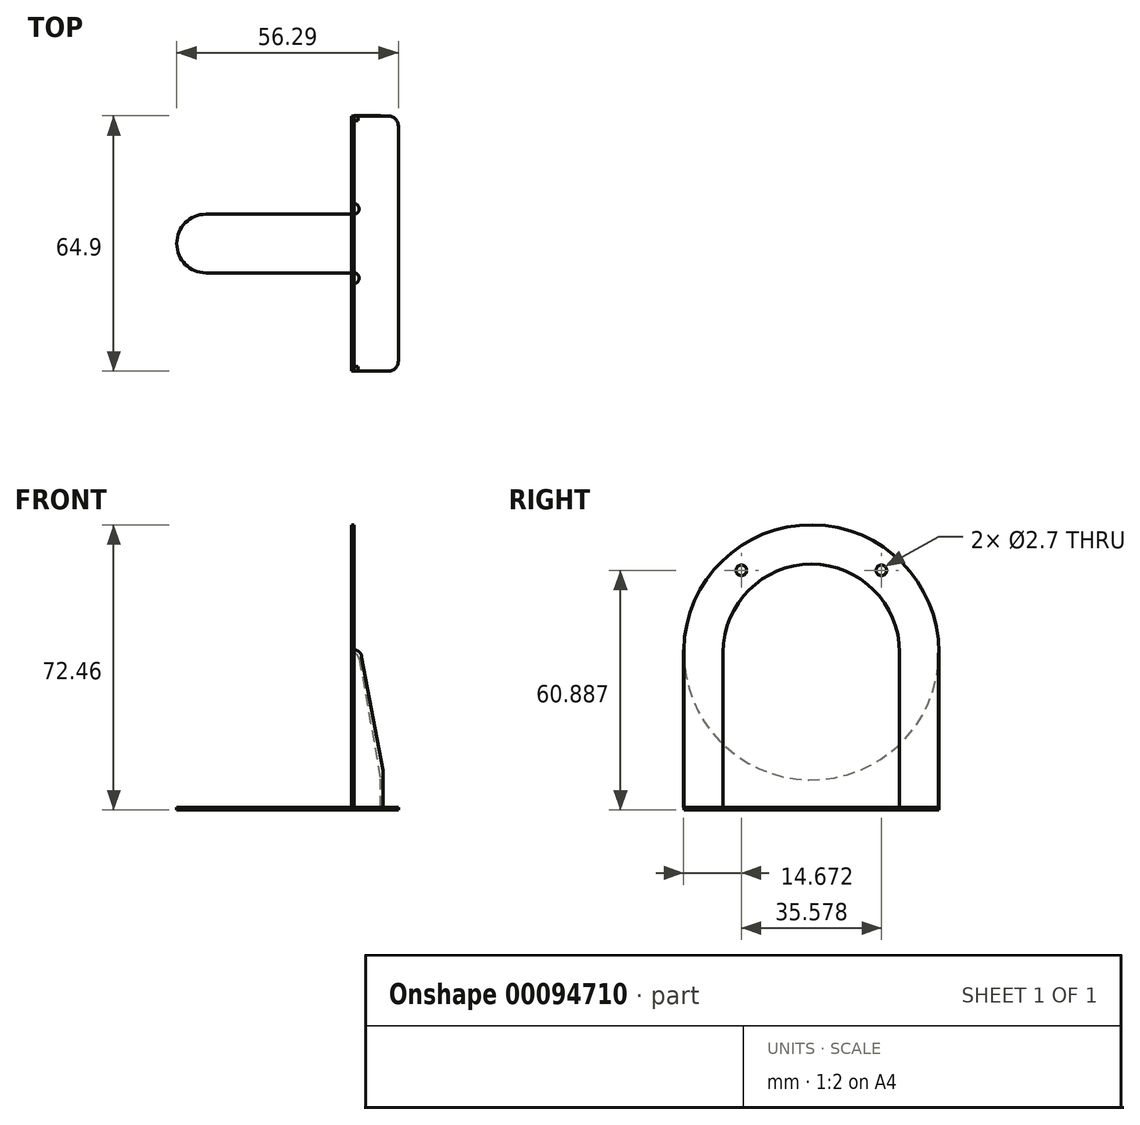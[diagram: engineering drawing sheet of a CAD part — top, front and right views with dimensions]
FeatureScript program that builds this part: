
annotation { "Feature Type Name" : "Feature", "Feature Type Description" : "" }
export const myFeature = defineFeature(function(context is Context, id is Id, definition is map)
    precondition{}
    {
        {
            var Q0;
            Q0=qCreatedBy(makeId("Top.planeOp"),FACE);
            var sketch = newSketch(context, id + "F0", { "sketchPlane" : qUnion([Q0])});
            skLineSegment(sketch, "E0", {"start": v(-33.32, 0) * mm, "end": v(45.54, 0) * mm, "construction": true});
            skLineSegment(sketch, "E1.bottom", {"start": v(-33.32, 0) * mm, "end": v(11.68, 0) * mm});
            skLineSegment(sketch, "E1.top", {"start": v(-33.32, -14.9) * mm, "end": v(11.68, -14.9) * mm});
            skLineSegment(sketch, "E1.left", {"start": v(-33.32, 0) * mm, "end": v(-33.32, -14.9) * mm});
            skLineSegment(sketch, "E1.right", {"start": v(11.68, 0) * mm, "end": v(11.68, -14.9) * mm});
            skLineSegment(sketch, "E2.bottom", {"start": v(11.68, 24.95) * mm, "end": v(22.97, 24.95) * mm});
            skLineSegment(sketch, "E2.top", {"start": v(11.68, -39.85) * mm, "end": v(22.97, -39.85) * mm});
            skLineSegment(sketch, "E2.right", {"start": v(22.97, 24.95) * mm, "end": v(22.97, -39.85) * mm});
            skLineSegment(sketch, "E3", {"start": v(11.68, 24.95) * mm, "end": v(11.68, 0) * mm});
            skLineSegment(sketch, "E4", {"start": v(11.68, -14.9) * mm, "end": v(11.68, -39.85) * mm});
            skSolve(sketch);
        }
        {
            var Q0;
            Q0=makeQuery(id+"F0.imprint","IMPRINT",FACE,{"disambiguationData":[TD([[makeQuery(id+"F0.imprint","IMPRINT",EDGE,{"derivedFrom":sQuery(id+"F0.wireOp",EDGE,"E1.bottom")}),-1.0]])]});
            extrude(context, id + "F1", {"entities" : qUnion([Q0]), "depth" : 0.63 * mm});
        }
        {
            var Q0;
            Q0=makeQuery(id+"F1.opExtrude","SWEPT_EDGE",EDGE,{"disambiguationData":[OSD([sQuery(id+"F0.wireOp",EDGE,"E1.bottom"),sQuery(id+"F0.wireOp",EDGE,"E1.left")])]});
            fillet(context, id + "F2", {"entities" : qUnion([Q0]), "radius" : 7.4 * mm, "tangentPropagation" : true, "allowEdgeOverflow" : false});
        }
        {
            var Q0;
            Q0=makeQuery(id+"F1.opExtrude","SWEPT_EDGE",EDGE,{"disambiguationData":[OSD([sQuery(id+"F0.wireOp",EDGE,"E1.top"),sQuery(id+"F0.wireOp",EDGE,"E1.left")])]});
            fillet(context, id + "F3", {"entities" : qUnion([Q0]), "radius" : 7.4 * mm, "tangentPropagation" : true, "allowEdgeOverflow" : false});
        }
        {
            var Q0;
            Q0=makeQuery(id+"F0.imprint","IMPRINT",FACE,{"disambiguationData":[TD([[makeQuery(id+"F0.imprint","IMPRINT",EDGE,{"derivedFrom":sQuery(id+"F0.wireOp",EDGE,"E1.right")}),1.0]])]});
            extrude(context, id + "F4", {"entities" : qUnion([Q0]), "operationType" : NewBodyOperationType.ADD, "depth" : 0.63 * mm});
        }
        {
            var Q0;
            {var subQ0=sQuery(id+"F0.wireOp",EDGE,"E1.right");Q0=makeQuery(id+"F4.boolean.opBoolean","MERGE",FACE,{"derivedFrom":[makeQuery(id+"F1.opExtrude","CAP_FACE",FACE,{"disambiguationData":[OSD([sQuery(id+"F0.wireOp",EDGE,"E1.bottom"),sQuery(id+"F0.wireOp",EDGE,"E1.top"),sQuery(id+"F0.wireOp",EDGE,"E1.left"),subQ0])],"isStart":false}),makeQuery(id+"F4.opExtrude","CAP_FACE",FACE,{"disambiguationData":[OSD([subQ0,sQuery(id+"F0.wireOp",EDGE,"E2.bottom"),sQuery(id+"F0.wireOp",EDGE,"E2.top"),sQuery(id+"F0.wireOp",EDGE,"E2.right"),sQuery(id+"F0.wireOp",EDGE,"E3"),sQuery(id+"F0.wireOp",EDGE,"E4")])],"isStart":false})]});}
            var sketch = newSketch(context, id + "F5", { "sketchPlane" : qUnion([Q0])});
            skLineSegment(sketch, "E5.bottom", {"start": v(11.68, -39.85) * mm, "end": v(12.78, -39.85) * mm});
            skLineSegment(sketch, "E5.top", {"start": v(11.68, -38.75) * mm, "end": v(12.78, -38.75) * mm});
            skLineSegment(sketch, "E5.left", {"start": v(11.68, -39.85) * mm, "end": v(11.68, -38.75) * mm});
            skLineSegment(sketch, "E5.right", {"start": v(12.78, -39.85) * mm, "end": v(12.78, -38.75) * mm});
            skLineSegment(sketch, "E6.bottom", {"start": v(11.68, 24.95) * mm, "end": v(12.78, 24.95) * mm});
            skLineSegment(sketch, "E6.top", {"start": v(11.68, 23.85) * mm, "end": v(12.78, 23.85) * mm});
            skLineSegment(sketch, "E6.left", {"start": v(11.68, 24.95) * mm, "end": v(11.68, 23.85) * mm});
            skLineSegment(sketch, "E6.right", {"start": v(12.78, 24.95) * mm, "end": v(12.78, 23.85) * mm});
            skArc(sketch, "E7", {"start": v(11.68, -17.6) * mm, "mid": v(13.03, -16.25) * mm, "end": v(11.68, -14.9) * mm});
            skArc(sketch, "E8", {"start": v(11.68, 0) * mm, "mid": v(13.03, 1.35) * mm, "end": v(11.68, 2.7) * mm});
            skSolve(sketch);
        }
        {
            var Q0;
            {var subQ0=sQuery(id+"F0.wireOp",EDGE,"E1.right");var subQ3=sQuery(id+"F0.wireOp",EDGE,"E1.bottom");var subQ4=sQuery(id+"F0.wireOp",EDGE,"E4");var subQ5=sQuery(id+"F0.wireOp",EDGE,"E3");Q0=makeQuery(id+"F4.boolean.opBoolean","SPLIT",FACE,{"disambiguationData":[TD([makeQuery(id+"F1.opExtrude","SWEPT_FACE",FACE,{"disambiguationData":[OSD([subQ3])]})])],"derivedFrom":makeQuery(id+"F4.opExtrude","SWEPT_FACE",FACE,{"disambiguationData":[OSD([subQ0,subQ5,subQ4])]})});}
            var sketch = newSketch(context, id + "F6", { "sketchPlane" : qUnion([Q0])});
            skLineSegment(sketch, "E9.bottom", {"start": v(39.85, 0) * mm, "end": v(29.85, 0) * mm});
            skLineSegment(sketch, "E9.top", {"start": v(39.85, 40.06) * mm, "end": v(29.85, 40.06) * mm});
            skLineSegment(sketch, "E9.left", {"start": v(39.85, 0) * mm, "end": v(39.85, 40.06) * mm});
            skLineSegment(sketch, "E9.right", {"start": v(29.85, 0) * mm, "end": v(29.85, 40.06) * mm});
            skLineSegment(sketch, "E10.bottom", {"start": v(-24.95, 0) * mm, "end": v(-14.95, 0) * mm});
            skLineSegment(sketch, "E10.top", {"start": v(-24.95, 40.06) * mm, "end": v(-14.95, 40.06) * mm});
            skLineSegment(sketch, "E10.left", {"start": v(-24.95, 0) * mm, "end": v(-24.95, 40.06) * mm});
            skLineSegment(sketch, "E10.right", {"start": v(-14.95, 0) * mm, "end": v(-14.95, 40.06) * mm});
            skArc(sketch, "E11", {"start": v(39.85, 40.06) * mm, "mid": v(7.45, 72.46) * mm, "end": v(-24.95, 40.06) * mm});
            skArc(sketch, "E12", {"start": v(29.85, 40.06) * mm, "mid": v(7.45, 62.46) * mm, "end": v(-14.95, 40.06) * mm});
            skSolve(sketch);
        }
        {
            var Q0;
            Q0=makeQuery(id+"F6.imprint","IMPRINT",FACE,{"disambiguationData":[TD([[makeQuery(id+"F6.imprint","IMPRINT",EDGE,{"derivedFrom":sQuery(id+"F6.wireOp",EDGE,"E9.bottom")}),-1.0]])]});
            var Q1;
            {var subQ0=sQuery(id+"F6.wireOp",EDGE,"E10.top");Q1=makeQuery(id+"F6.imprint","IMPRINT",FACE,{"disambiguationData":[TD([[makeQuery(id+"F6.imprint","IMPRINT",EDGE,{"derivedFrom":subQ0}),-1.0]])]});}
            extrude(context, id + "F7", {"entities" : qUnion([Q0, Q1]), "operationType" : NewBodyOperationType.ADD, "depth" : 0.63 * mm});
        }
        {
            var Q0;
            Q0 = qSketchRegion(id + "F6", true);
            extrude(context, id + "F8", {"entities" : qUnion([Q0]), "operationType" : NewBodyOperationType.ADD, "depth" : 0.63 * mm});
        }
        {
            var Q0;
            Q0=makeQuery(id+"F7.boolean.opBoolean","MERGE",FACE,{"derivedFrom":[makeQuery(id+"F4.opExtrude","SWEPT_FACE",FACE,{"disambiguationData":[OSD([sQuery(id+"F0.wireOp",EDGE,"E2.top")])]}),makeQuery(id+"F7.opExtrude","SWEPT_FACE",FACE,{"disambiguationData":[OSD([sQuery(id+"F6.wireOp",EDGE,"E9.left")])]})]});
            var sketch = newSketch(context, id + "F9", { "sketchPlane" : qUnion([Q0])});
            skLineSegment(sketch, "E13", {"start": v(11.68, 0.63) * mm, "end": v(11.68, 40.7) * mm});
            skLineSegment(sketch, "E14", {"start": v(19.08, 0) * mm, "end": v(19.08, 10.06) * mm});
            skPoint(sketch, "E15", {"position": v(11.68, 36.69) * mm});
            skPoint(sketch, "E16", {"position": v(11.68, 36.7) * mm});
            skArc(sketch, "E17", {"start": v(11.68, 36.7) * mm, "mid": v(13.7, 38.7) * mm, "end": v(11.68, 40.7) * mm});
            skLineSegment(sketch, "E18", {"start": v(13.7, 38.7) * mm, "end": v(19.08, 10.06) * mm});
            skSolve(sketch);
        }
        {
            var Q0;
            {var subQ0=sQuery(id+"F9.wireOp",EDGE,"E18");Q0=makeQuery(id+"F9.imprint","IMPRINT",FACE,{"disambiguationData":[TD([[makeQuery(id+"F9.imprint","IMPRINT",EDGE,{"derivedFrom":subQ0}),-1.0]])]});}
            var Q1;
            {var subQ0=sQuery(id+"F9.wireOp",EDGE,"E13");var subQ5=sQuery(id+"F9.wireOp",EDGE,"E17");var subQ6=makeQuery(id+"F9.imprint","INTERSECT",VERTEX,{"disambiguationData":[OD(1.0)],"derivedFrom":[subQ0,subQ5]});Q1=makeQuery(id+"F9.imprint","IMPRINT",FACE,{"disambiguationData":[TD([[makeQuery(id+"F9.imprint","IMPRINT",EDGE,{"disambiguationData":[TD([[subQ6,-1.0]])],"derivedFrom":subQ5}),1.0]])]});}
            extrude(context, id + "F10", {"entities" : qUnion([Q0, Q1]), "operationType" : NewBodyOperationType.ADD, "endBound" : BoundingType.SYMMETRIC, "oppositeDirection" : true, "depth" : 0.1 * mm});
        }
        {
            var Q0;
            Q0=makeQuery(id+"F4.opExtrude","SWEPT_EDGE",EDGE,{"disambiguationData":[OSD([sQuery(id+"F0.wireOp",EDGE,"E2.top"),sQuery(id+"F0.wireOp",EDGE,"E2.right")])]});
            var Q1;
            Q1=makeQuery(id+"F4.opExtrude","SWEPT_EDGE",EDGE,{"disambiguationData":[OSD([sQuery(id+"F0.wireOp",EDGE,"E2.bottom"),sQuery(id+"F0.wireOp",EDGE,"E2.right")])]});
            fillet(context, id + "F11", {"entities" : qUnion([Q0, Q1]), "radius" : 2.5 * mm, "tangentPropagation" : true, "allowEdgeOverflow" : false});
        }
        {
            var Q0;
            {var subQ0=sQuery(id+"F6.wireOp",EDGE,"E10.left");Q0=makeQuery(id+"F8.boolean.opBoolean","MERGE",FACE,{"derivedFrom":[makeQuery(id+"F4.opExtrude","SWEPT_FACE",FACE,{"disambiguationData":[OSD([sQuery(id+"F0.wireOp",EDGE,"E2.bottom")])]}),makeQuery(id+"F7.opExtrude","SWEPT_FACE",FACE,{"disambiguationData":[OSD([subQ0])]}),makeQuery(id+"F8.opExtrude","SWEPT_FACE",FACE,{"disambiguationData":[OSD([subQ0])]})]});}
            var sketch = newSketch(context, id + "F12", { "sketchPlane" : qUnion([Q0])});
            skLineSegment(sketch, "E19", {"start": v(-11.05, 0) * mm, "end": v(-11.05, 40.06) * mm});
            skLineSegment(sketch, "E20", {"start": v(-18.45, 0) * mm, "end": v(-18.45, 7.85) * mm});
            skArc(sketch, "E21", {"start": v(-11.05, 40.06) * mm, "mid": v(-13.03, 38.38) * mm, "end": v(-11.68, 36.16) * mm});
            skLineSegment(sketch, "E22", {"start": v(-13.03, 38.38) * mm, "end": v(-18.45, 7.85) * mm});
            skSolve(sketch);
        }
        {
            var Q0;
            {var subQ6=sQuery(id+"F12.wireOp",EDGE,"E22");Q0=makeQuery(id+"F12.imprint","IMPRINT",FACE,{"disambiguationData":[TD([[makeQuery(id+"F12.imprint","IMPRINT",EDGE,{"derivedFrom":subQ6}),1.0]])]});}
            var Q1;
            {var subQ0=sQuery(id+"F12.wireOp",EDGE,"E21");var subQ1=makeQuery(id+"F12.imprint","INTERSECT",VERTEX,{"derivedFrom":[subQ0,sQuery(id+"F12.wireOp",EDGE,"E22")]});Q1=makeQuery(id+"F12.imprint","IMPRINT",FACE,{"disambiguationData":[TD([[makeQuery(id+"F12.imprint","IMPRINT",EDGE,{"disambiguationData":[TD([[subQ1,1.0]])],"derivedFrom":subQ0}),1.0]])]});}
            extrude(context, id + "F13", {"entities" : qUnion([Q0, Q1]), "operationType" : NewBodyOperationType.ADD, "endBound" : BoundingType.SYMMETRIC, "depth" : 0.1 * mm});
        }
        {
            var Q0;
            {var subQ0=sQuery(id+"F6.wireOp",EDGE,"E10.right");var subQ1=sQuery(id+"F6.wireOp",EDGE,"E10.left");var subQ2=sQuery(id+"F6.wireOp",EDGE,"E9.right");var subQ3=sQuery(id+"F6.wireOp",EDGE,"E9.left");var subQ4=sQuery(id+"F6.wireOp",EDGE,"E9.bottom");Q0=makeQuery(id+"F8.boolean.opBoolean","MERGE",FACE,{"derivedFrom":[makeQuery(id+"F7.opExtrude","CAP_FACE",FACE,{"disambiguationData":[OSD([sQuery(id+"F0.wireOp",EDGE,"E1.right"),sQuery(id+"F0.wireOp",EDGE,"E3"),sQuery(id+"F0.wireOp",EDGE,"E4"),sQuery(id+"F6.wireOp",EDGE,"E10.top"),subQ1,subQ0])],"isStart":true}),makeQuery(id+"F7.opExtrude","CAP_FACE",FACE,{"disambiguationData":[OSD([subQ4,sQuery(id+"F6.wireOp",EDGE,"E9.top"),subQ3,subQ2])],"isStart":true}),makeQuery(id+"F8.opExtrude","CAP_FACE",FACE,{"disambiguationData":[OSD([subQ4,subQ3,subQ2,sQuery(id+"F6.wireOp",EDGE,"E10.bottom"),subQ1,subQ0,sQuery(id+"F6.wireOp",EDGE,"E11"),sQuery(id+"F6.wireOp",EDGE,"E12")])],"isStart":true})]});}
            var sketch = newSketch(context, id + "F14", { "sketchPlane" : qUnion([Q0])});
            skPoint(sketch, "E23", {"position": v(-25.23, 60.89) * mm});
            skPoint(sketch, "E24", {"position": v(10.35, 60.89) * mm});
            skLineSegment(sketch, "E25", {"start": v(-29.2, 64.07) * mm, "end": v(-21.25, 57.7) * mm, "construction": true});
            skLineSegment(sketch, "E26", {"start": v(7.4, 56.83) * mm, "end": v(13.3, 64.94) * mm, "construction": true});
            skSolve(sketch);
        }
        {
            var Q0;
            Q0=sQuery(id+"F14.wireOp",VERTEX,"E23");
            var Q1;
            Q1=sQuery(id+"F14.wireOp",VERTEX,"E24");
            var Q2;
            Q2=makeQuery(id+"F1.opExtrude","SWEPT_BODY",BODY,{"disambiguationData":[OSD([sQuery(id+"F0.wireOp",EDGE,"E1.bottom"),sQuery(id+"F0.wireOp",EDGE,"E1.top"),sQuery(id+"F0.wireOp",EDGE,"E1.left"),sQuery(id+"F0.wireOp",EDGE,"E1.right")])]});
            hole(context, id + "F15", {"style" : HoleStyle.SIMPLE, "endStyle" : HoleEndStyle.THROUGH, "holeDiameter" : 2.7 * mm, "locations" : qUnion([Q0, Q1]), "scope" : qUnion([Q2]), "isTappedThrough" : true});
        }
        {
            var Q0;
            Q0=makeQuery(id+"F5.imprint","IMPRINT",FACE,{"disambiguationData":[TD([[makeQuery(id+"F5.imprint","IMPRINT",EDGE,{"derivedFrom":sQuery(id+"F5.wireOp",EDGE,"E6.bottom")}),-1.0]])]});
            var Q1;
            {var subQ0=sQuery(id+"F5.wireOp",EDGE,"E8");Q1=makeQuery(id+"F5.imprint","IMPRINT",FACE,{"disambiguationData":[TD([[makeQuery(id+"F5.imprint","IMPRINT",EDGE,{"derivedFrom":subQ0}),1.0]])]});}
            var Q2;
            {var subQ0=sQuery(id+"F5.wireOp",EDGE,"E7");Q2=makeQuery(id+"F5.imprint","IMPRINT",FACE,{"disambiguationData":[TD([[makeQuery(id+"F5.imprint","IMPRINT",EDGE,{"derivedFrom":subQ0}),1.0]])]});}
            var Q3;
            Q3=makeQuery(id+"F5.imprint","IMPRINT",FACE,{"disambiguationData":[TD([[makeQuery(id+"F5.imprint","IMPRINT",EDGE,{"derivedFrom":sQuery(id+"F5.wireOp",EDGE,"E5.bottom")}),1.0]])]});
            extrude(context, id + "F16", {"entities" : qUnion([Q0, Q1, Q2, Q3]), "operationType" : NewBodyOperationType.REMOVE, "endBound" : BoundingType.THROUGH_ALL, "oppositeDirection" : true, "depth" : 25 * mm});
        }
    });
